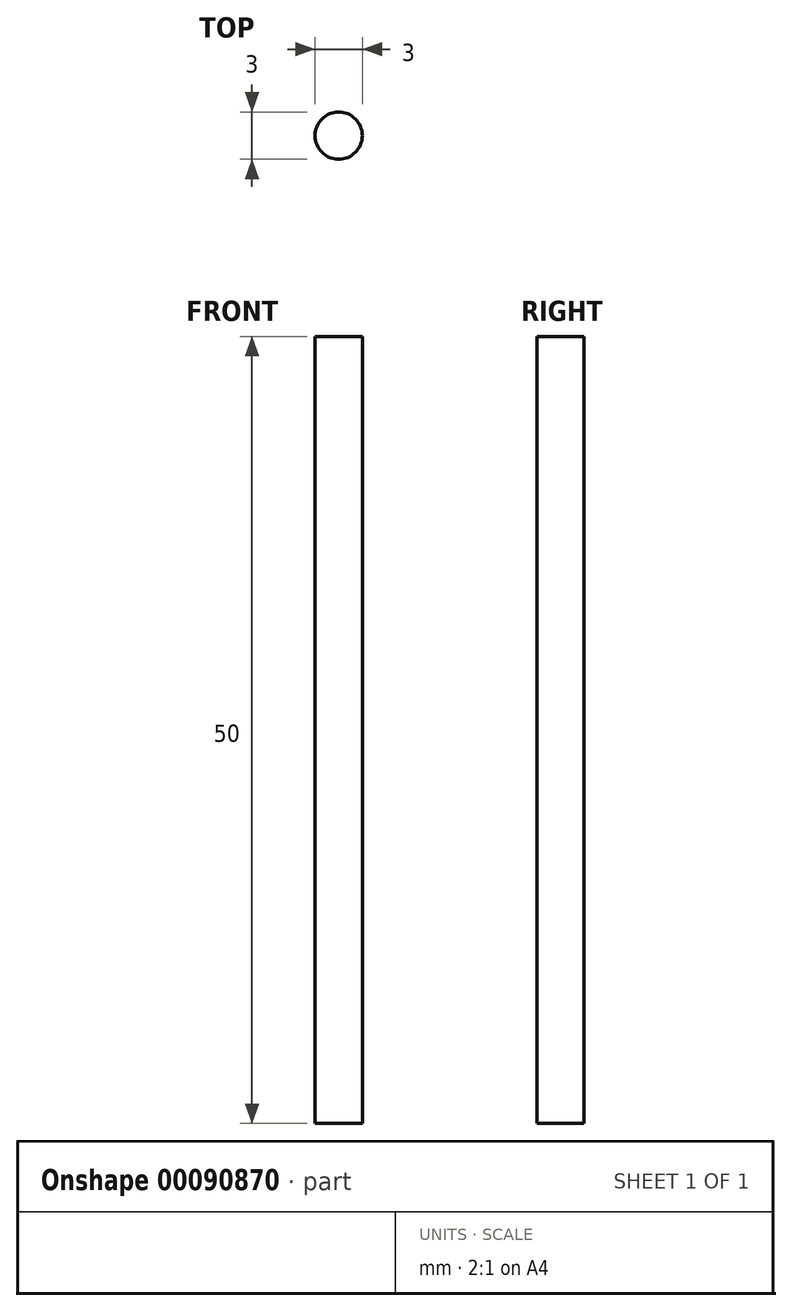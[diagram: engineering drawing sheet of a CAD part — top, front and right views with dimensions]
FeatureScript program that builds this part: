
annotation { "Feature Type Name" : "Feature", "Feature Type Description" : "" }
export const myFeature = defineFeature(function(context is Context, id is Id, definition is map)
    precondition{}
    {
        {
            var Q0;
            Q0=qCreatedBy(makeId("Top.planeOp"),FACE);
            var sketch = newSketch(context, id + "F0", { "sketchPlane" : qUnion([Q0])});
            skCircle(sketch, "E0", {"center": v(0, 0) * mm, "radius": 1.5 * mm});
            skSolve(sketch);
        }
        {
            var Q0;
            Q0=makeQuery(id+"F0.imprint","IMPRINT",FACE,{"disambiguationData":[TD([[makeQuery(id+"F0.imprint","IMPRINT",EDGE,{"derivedFrom":sQuery(id+"F0.wireOp",EDGE,"E0")}),1.0]])]});
            extrude(context, id + "F1", {"entities" : qUnion([Q0]), "depth" : 25 * mm, "hasSecondDirection" : true, "secondDirectionOppositeDirection" : true, "secondDirectionDepth" : 25 * mm});
        }
    });
